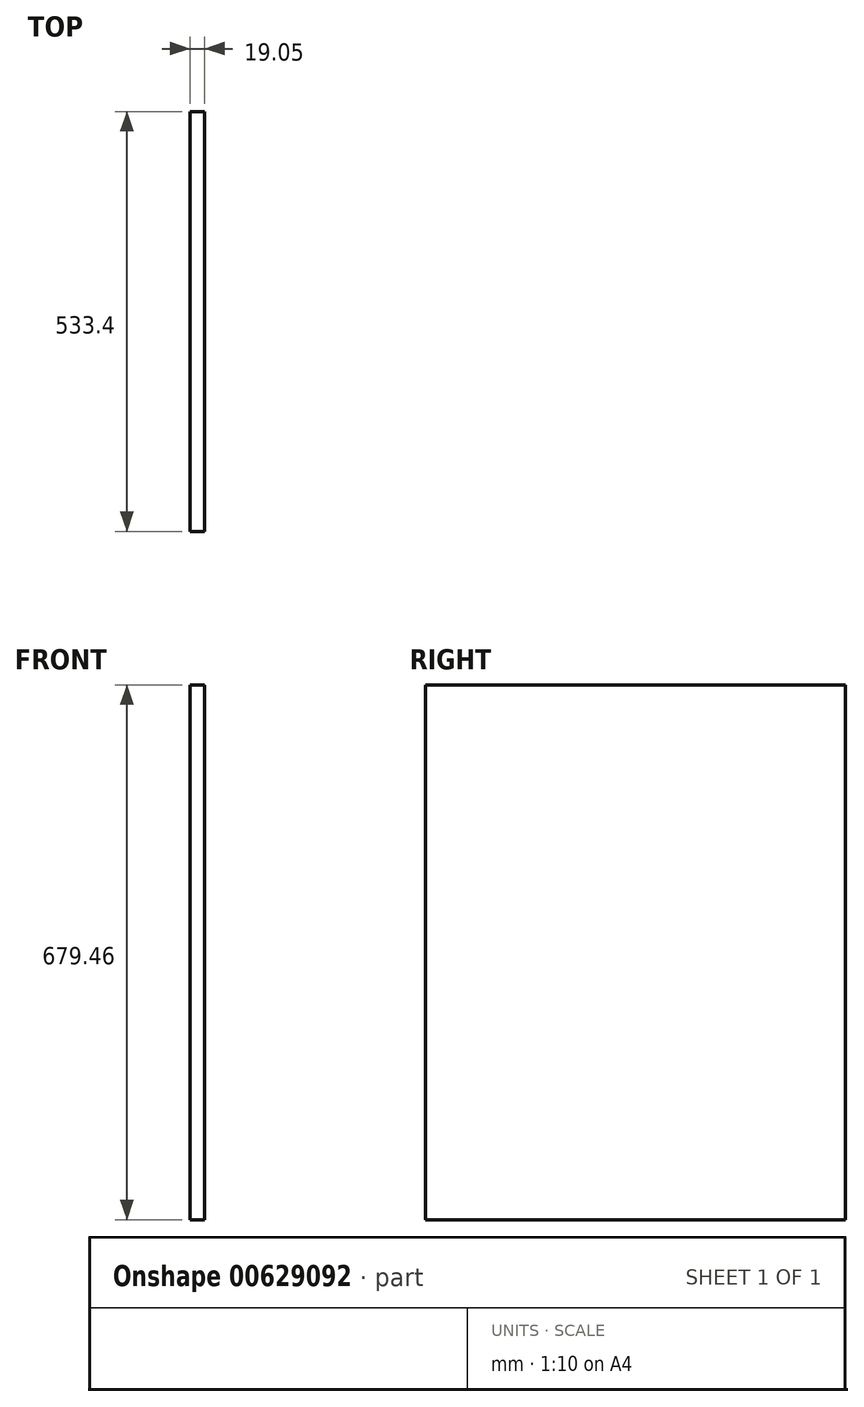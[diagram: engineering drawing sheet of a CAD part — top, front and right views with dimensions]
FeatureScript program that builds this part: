
annotation { "Feature Type Name" : "Feature", "Feature Type Description" : "" }
export const myFeature = defineFeature(function(context is Context, id is Id, definition is map)
    precondition{}
    {
        {
            var Q0;
            Q0=qCreatedBy(makeId("Right.planeOp"),FACE);
            var sketch = newSketch(context, id + "F0", { "sketchPlane" : qUnion([Q0])});
            skLineSegment(sketch, "E0.bottom", {"start": v(266.7, 339.73) * mm, "end": v(-266.7, 339.73) * mm});
            skLineSegment(sketch, "E0.top", {"start": v(266.7, -339.73) * mm, "end": v(-266.7, -339.73) * mm});
            skLineSegment(sketch, "E0.left", {"start": v(266.7, 339.72) * mm, "end": v(266.7, -339.73) * mm});
            skLineSegment(sketch, "E0.right", {"start": v(-266.7, 339.73) * mm, "end": v(-266.7, -339.73) * mm});
            skPoint(sketch, "E0.middle", {"position": v(0, 0) * mm});
            skSolve(sketch);
        }
        {
            var Q0;
            Q0=makeQuery(id+"F0.imprint","IMPRINT",FACE,{"disambiguationData":[TD([[makeQuery(id+"F0.imprint","IMPRINT",EDGE,{"derivedFrom":sQuery(id+"F0.wireOp",EDGE,"E0.bottom")}),1.0]])]});
            extrude(context, id + "F1", {"entities" : qUnion([Q0]), "depth" : 19.05 * mm, "offsetDistance" : 25.4 * mm});
        }
    });
